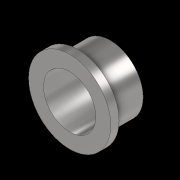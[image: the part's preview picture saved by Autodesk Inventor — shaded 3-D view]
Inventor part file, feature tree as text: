
AUTODESK INVENTOR PART (.ipt)
format: ipt  version: 2022.2 (Build 262287010, 287A)  size: 150,528 bytes
history: native  units: mm
features: extrude x2, sketch x2
ambient origin geometry x8: Origin, YZ Plane, XZ Plane, XY Plane, X Axis, Y Axis, Z Axis, Center Point
bodies: Solid1 (feature_tree)
feature tree (4):
  extrude  "Extrusion1"  Depth=6.3mm
  extrude  "Extrusion2"  Depth=1.0mm
  sketch  "Sketch1"  dims[d0=7.9mm d1=6.3mm]
  sketch  "Sketch2"  dims[d2=4.9mm d3=0.0mm d4=9.9mm d5=1.0mm d6=0.0mm]
